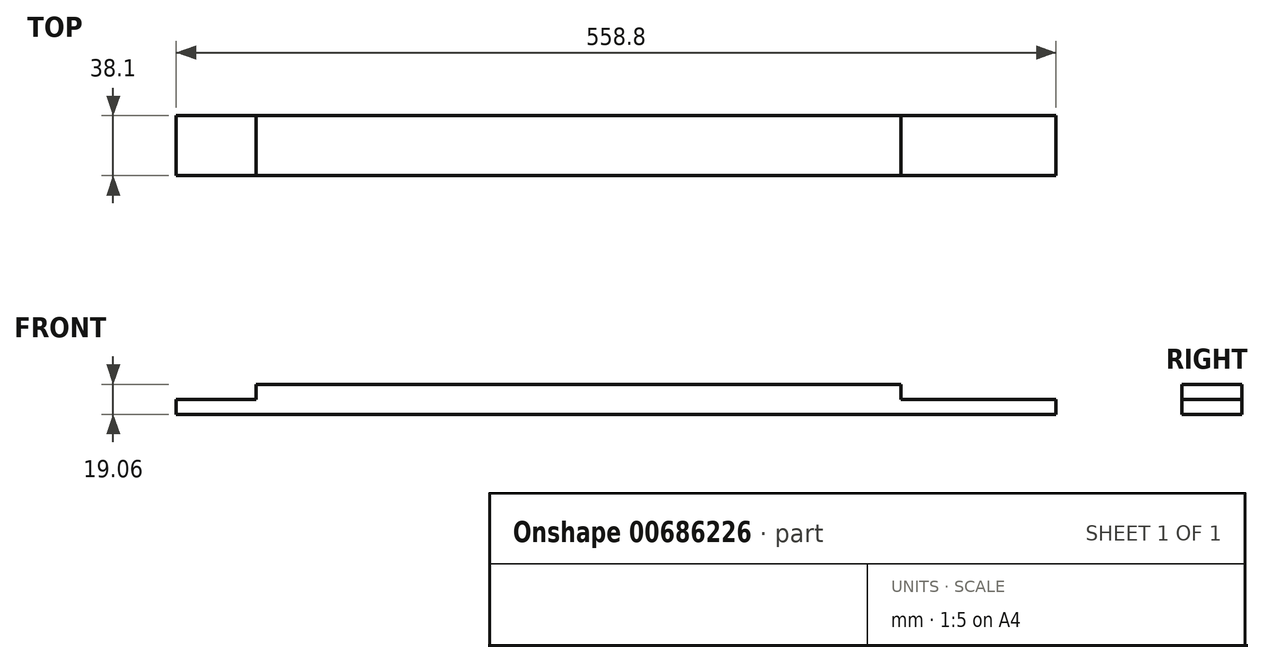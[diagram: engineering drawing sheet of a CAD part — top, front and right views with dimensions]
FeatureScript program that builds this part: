
annotation { "Feature Type Name" : "Feature", "Feature Type Description" : "" }
export const myFeature = defineFeature(function(context is Context, id is Id, definition is map)
    precondition{}
    {
        {
            var Q0;
            Q0=qCreatedBy(makeId("Top.planeOp"),FACE);
            var sketch = newSketch(context, id + "F0", { "sketchPlane" : qUnion([Q0])});
            skLineSegment(sketch, "E0.bottom", {"start": v(-204.79, 19.05) * mm, "end": v(204.79, 19.05) * mm});
            skLineSegment(sketch, "E0.top", {"start": v(-204.79, -19.05) * mm, "end": v(204.79, -19.05) * mm});
            skLineSegment(sketch, "E0.left", {"start": v(-204.79, 19.05) * mm, "end": v(-204.79, -19.05) * mm});
            skLineSegment(sketch, "E0.right", {"start": v(204.79, 19.05) * mm, "end": v(204.79, -19.05) * mm});
            skPoint(sketch, "E0.middle", {"position": v(0, 0) * mm});
            skSolve(sketch);
        }
        {
            var Q0;
            Q0=qSketchRegion(id+"F0",true);
            extrude(context, id + "F1", {"entities" : qUnion([Q0]), "endBound" : BoundingType.SYMMETRIC, "depth" : 19.05 * mm, "offsetDistance" : 25.4 * mm});
        }
        {
            var Q0;
            Q0=qCreatedBy(makeId("Top.planeOp"),FACE);
            var sketch = newSketch(context, id + "F2", { "sketchPlane" : qUnion([Q0])});
            skLineSegment(sketch, "E1.bottom", {"start": v(-204.79, -19.05) * mm, "end": v(-255.59, -19.05) * mm});
            skLineSegment(sketch, "E1.top", {"start": v(-204.79, 19.05) * mm, "end": v(-255.59, 19.05) * mm});
            skLineSegment(sketch, "E1.left", {"start": v(-204.79, 19.05) * mm, "end": v(-204.79, -19.05) * mm});
            skLineSegment(sketch, "E1.right", {"start": v(-255.59, 19.05) * mm, "end": v(-255.59, -19.05) * mm});
            skLineSegment(sketch, "E2.bottom", {"start": v(204.79, -19.05) * mm, "end": v(303.21, -19.05) * mm});
            skLineSegment(sketch, "E2.top", {"start": v(204.79, 19.05) * mm, "end": v(303.21, 19.05) * mm});
            skLineSegment(sketch, "E2.left", {"start": v(204.79, 19.05) * mm, "end": v(204.79, -19.05) * mm});
            skLineSegment(sketch, "E2.right", {"start": v(303.21, 19.05) * mm, "end": v(303.21, -19.05) * mm});
            skSolve(sketch);
        }
        {
            var Q0;
            Q0 = qSketchRegion(id + "F2", true);
            var Q1;
            Q1=makeQuery(id+"F1.opExtrude","CAP_FACE",FACE,{"disambiguationData":[OSD([sQuery(id+"F0.wireOp",EDGE,"E0.bottom"),sQuery(id+"F0.wireOp",EDGE,"E0.top"),sQuery(id+"F0.wireOp",EDGE,"E0.left"),sQuery(id+"F0.wireOp",EDGE,"E0.right")])],"isStart":true});
            extrude(context, id + "F3", {"entities" : qUnion([Q0]), "operationType" : NewBodyOperationType.ADD, "endBound" : BoundingType.UP_TO_SURFACE, "oppositeDirection" : true, "depth" : 6.35 * mm, "endBoundEntityFace" : qUnion([Q1]), "offsetDistance" : 25.4 * mm});
        }
    });
